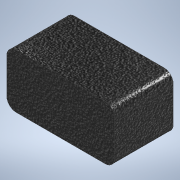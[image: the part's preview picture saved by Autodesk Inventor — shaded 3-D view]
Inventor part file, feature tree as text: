
AUTODESK INVENTOR PART (.ipt)
format: ipt  version: 2020 (Build 240168000, 168)  size: 118,784 bytes
history: native  units: in
note: dims shown in document units (in); Inventor stores cm internally (conversion verified against a paired STEP export)
features: extrude x1, fillet x1, sketch x1
ambient origin geometry x8: Origin, YZ Plane, XZ Plane, XY Plane, X Axis, Y Axis, Z Axis, Center Point
bodies: Solid1 (feature_tree)
feature tree (3):
  extrude  "Extrusion1"  Depth=0.9843in
  fillet  "Fillet1"  Radius=0.9055in
  sketch  "Sketch1"  dims[d0=1.811in d1=0.9843in d2=0.9055in d3=0.0in d4=0.1575in]
